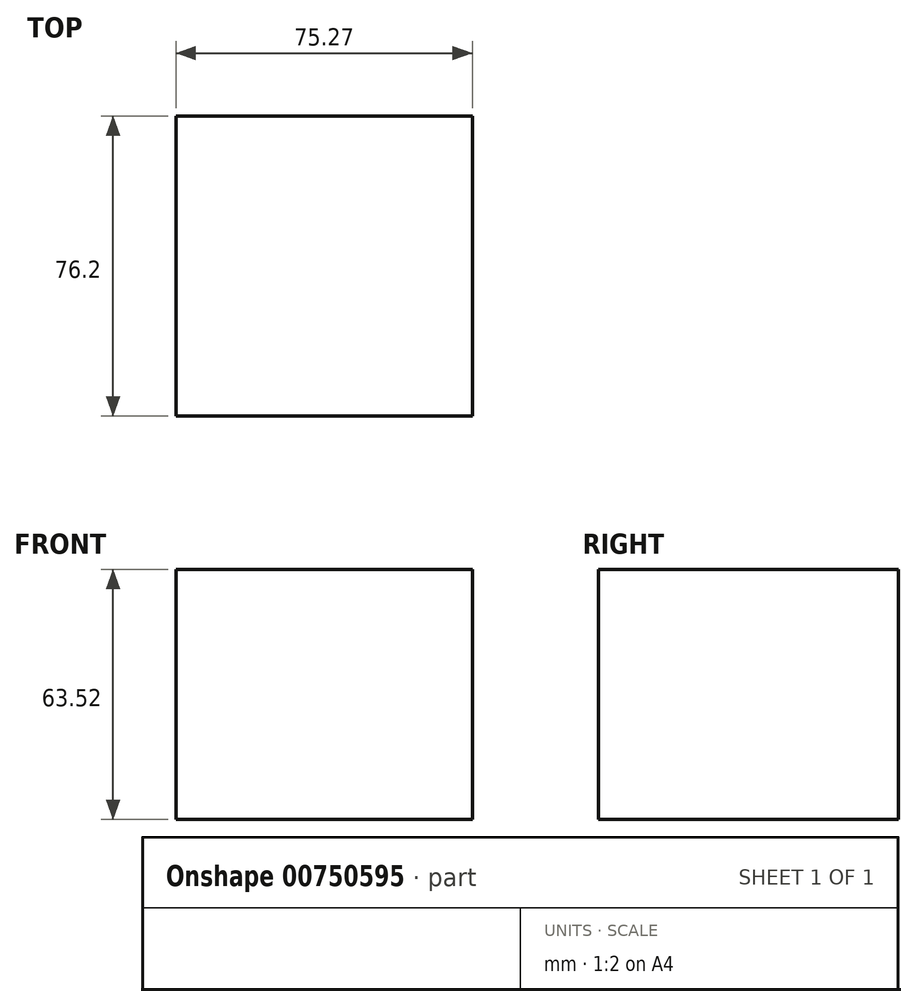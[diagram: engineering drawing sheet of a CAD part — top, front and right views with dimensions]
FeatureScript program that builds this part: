
annotation { "Feature Type Name" : "Feature", "Feature Type Description" : "" }
export const myFeature = defineFeature(function(context is Context, id is Id, definition is map)
    precondition{}
    {
        {
            var Q0;
            Q0=qCreatedBy(makeId("Front.planeOp"),FACE);
            var sketch = newSketch(context, id + "F0", { "sketchPlane" : qUnion([Q0])});
            skLineSegment(sketch, "E0.bottom", {"start": v(-32.7, -26.83) * mm, "end": v(42.56, -26.83) * mm});
            skLineSegment(sketch, "E0.top", {"start": v(-32.7, 36.69) * mm, "end": v(42.56, 36.69) * mm});
            skLineSegment(sketch, "E0.left", {"start": v(-32.7, -26.83) * mm, "end": v(-32.7, 36.69) * mm});
            skLineSegment(sketch, "E0.right", {"start": v(42.56, -26.83) * mm, "end": v(42.56, 36.69) * mm});
            skLineSegment(sketch, "E1.bottom", {"start": v(-111.2, -28.16) * mm, "end": v(-107.79, -28.16) * mm});
            skLineSegment(sketch, "E1.top", {"start": v(-111.2, -28.53) * mm, "end": v(-107.79, -28.53) * mm});
            skLineSegment(sketch, "E1.left", {"start": v(-111.2, -28.16) * mm, "end": v(-111.2, -28.53) * mm});
            skLineSegment(sketch, "E1.right", {"start": v(-107.79, -28.16) * mm, "end": v(-107.79, -28.53) * mm});
            skSolve(sketch);
        }
        {
            var Q0;
            Q0=makeQuery(id+"F0.imprint","IMPRINT",FACE,{"disambiguationData":[TD([[makeQuery(id+"F0.imprint","IMPRINT",EDGE,{"derivedFrom":sQuery(id+"F0.wireOp",EDGE,"E0.bottom")}),1.0]])]});
            extrude(context, id + "F1", {"entities" : qUnion([Q0]), "depth" : 76.2 * mm, "offsetDistance" : 25.4 * mm});
        }
    });
